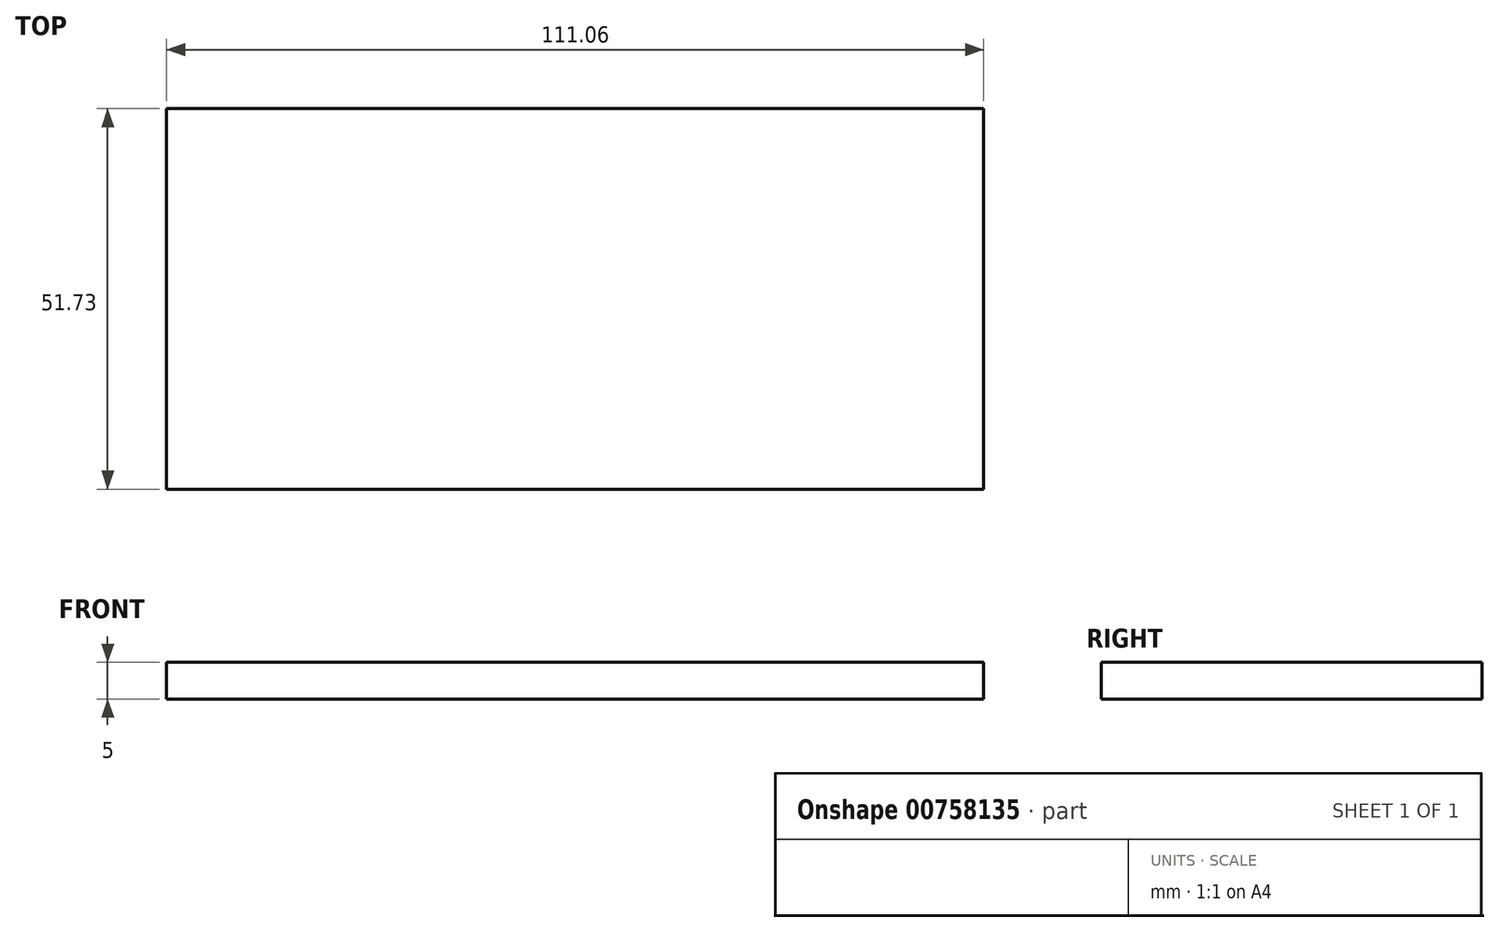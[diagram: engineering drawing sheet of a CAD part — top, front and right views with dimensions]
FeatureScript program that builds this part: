
annotation { "Feature Type Name" : "Feature", "Feature Type Description" : "" }
export const myFeature = defineFeature(function(context is Context, id is Id, definition is map)
    precondition{}
    {
        {
            var Q0;
            Q0=qCreatedBy(makeId("Top.planeOp"),FACE);
            var sketch = newSketch(context, id + "F0", { "sketchPlane" : qUnion([Q0])});
            skLineSegment(sketch, "E0.bottom", {"start": v(-49.16, 40.91) * mm, "end": v(61.9, 40.91) * mm});
            skLineSegment(sketch, "E0.top", {"start": v(-49.16, -10.82) * mm, "end": v(61.9, -10.82) * mm});
            skLineSegment(sketch, "E0.left", {"start": v(-49.16, 40.91) * mm, "end": v(-49.16, -10.82) * mm});
            skLineSegment(sketch, "E0.right", {"start": v(61.9, 40.91) * mm, "end": v(61.9, -10.82) * mm});
            skSolve(sketch);
        }
        {
            var Q0;
            Q0 = qSketchRegion(id + "F0", true);
            extrude(context, id + "F1", {"entities" : qUnion([Q0]), "depth" : 5 * mm, "offsetDistance" : 25 * mm});
        }
    });
